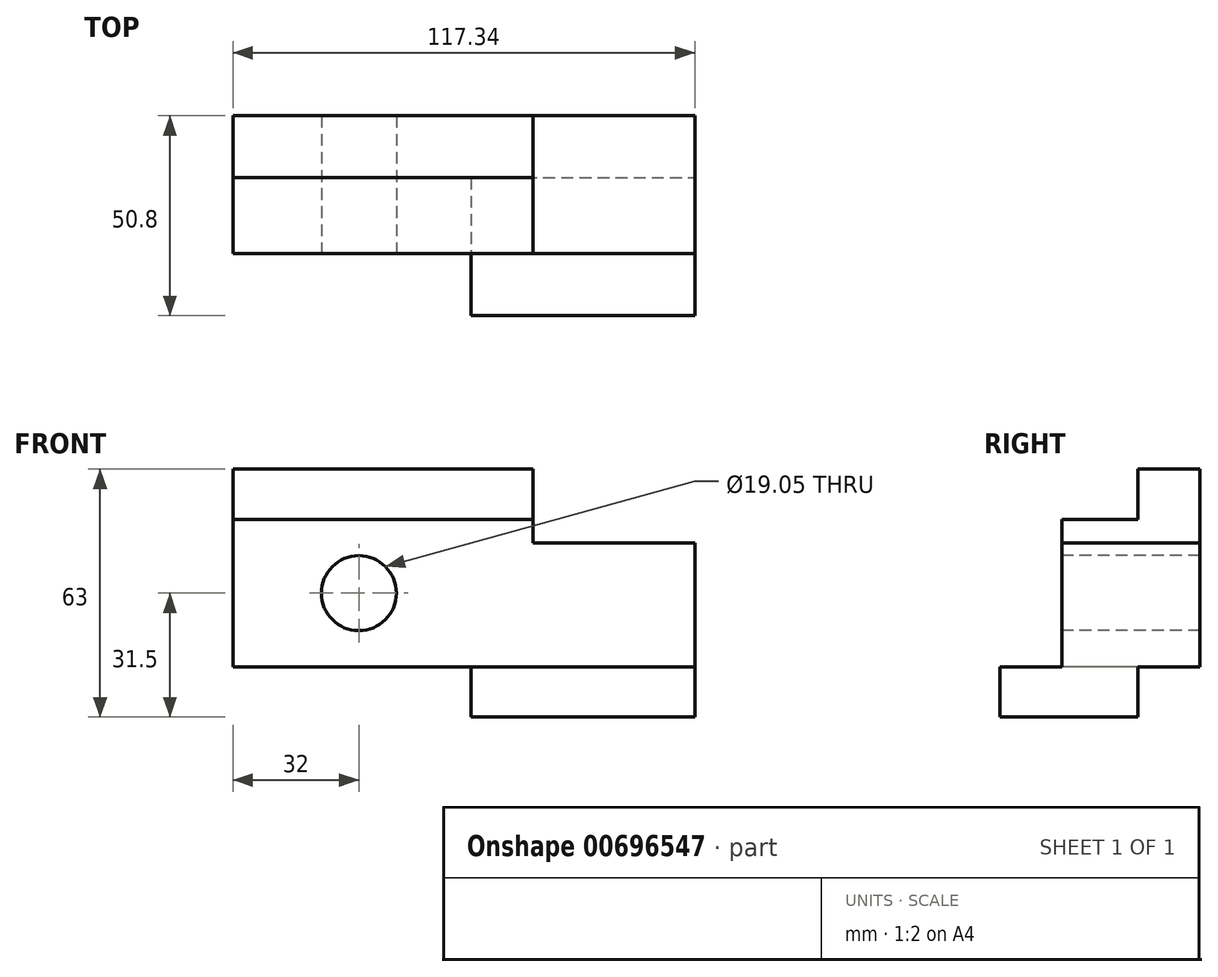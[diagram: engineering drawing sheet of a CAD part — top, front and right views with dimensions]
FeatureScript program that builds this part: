
annotation { "Feature Type Name" : "Feature", "Feature Type Description" : "" }
export const myFeature = defineFeature(function(context is Context, id is Id, definition is map)
    precondition{}
    {
        {
            var Q0;
            Q0=qCreatedBy(makeId("Front.planeOp"),FACE);
            var sketch = newSketch(context, id + "F0", { "sketchPlane" : qUnion([Q0])});
            skLineSegment(sketch, "E0.bottom", {"start": v(-58.67, 31.5) * mm, "end": v(58.67, 31.5) * mm});
            skLineSegment(sketch, "E0.top", {"start": v(-58.67, -31.5) * mm, "end": v(58.67, -31.5) * mm});
            skLineSegment(sketch, "E0.left", {"start": v(-58.67, 31.5) * mm, "end": v(-58.67, -31.5) * mm});
            skLineSegment(sketch, "E0.right", {"start": v(58.67, 31.5) * mm, "end": v(58.67, -31.5) * mm});
            skPoint(sketch, "E0.middle", {"position": v(0, 0) * mm});
            skSolve(sketch);
        }
        {
            var Q0;
            Q0=makeQuery(id+"F0.imprint","IMPRINT",FACE,{"disambiguationData":[TD([[makeQuery(id+"F0.imprint","IMPRINT",EDGE,{"derivedFrom":sQuery(id+"F0.wireOp",EDGE,"E0.bottom")}),-1.0]])]});
            extrude(context, id + "F1", {"entities" : qUnion([Q0]), "depth" : 50.8 * mm, "offsetDistance" : 25.4 * mm});
        }
        {
            var Q0;
            Q0=makeQuery(id+"F1.opExtrude","CAP_FACE",FACE,{"disambiguationData":[OSD([sQuery(id+"F0.wireOp",EDGE,"E0.bottom"),sQuery(id+"F0.wireOp",EDGE,"E0.top"),sQuery(id+"F0.wireOp",EDGE,"E0.left"),sQuery(id+"F0.wireOp",EDGE,"E0.right")])],"isStart":false});
            var sketch = newSketch(context, id + "F2", { "sketchPlane" : qUnion([Q0])});
            skLineSegment(sketch, "E1.bottom", {"start": v(58.67, 31.5) * mm, "end": v(17.53, 31.5) * mm});
            skLineSegment(sketch, "E1.top", {"start": v(58.67, 12.7) * mm, "end": v(17.53, 12.7) * mm});
            skLineSegment(sketch, "E1.left", {"start": v(58.67, 31.5) * mm, "end": v(58.67, 12.7) * mm});
            skLineSegment(sketch, "E1.right", {"start": v(17.53, 31.5) * mm, "end": v(17.53, 12.7) * mm});
            skSolve(sketch);
        }
        {
            var Q0;
            Q0=makeQuery(id+"F2.imprint","IMPRINT",FACE,{"disambiguationData":[TD([[makeQuery(id+"F2.imprint","IMPRINT",EDGE,{"derivedFrom":sQuery(id+"F2.wireOp",EDGE,"E1.bottom")}),-1.0]])]});
            extrude(context, id + "F3", {"entities" : qUnion([Q0]), "operationType" : NewBodyOperationType.REMOVE, "endBound" : BoundingType.THROUGH_ALL, "oppositeDirection" : true, "depth" : 25.4 * mm, "offsetDistance" : 25.4 * mm});
        }
        {
            var Q0;
            Q0=makeQuery(id+"F1.opExtrude","CAP_FACE",FACE,{"disambiguationData":[OSD([sQuery(id+"F0.wireOp",EDGE,"E0.bottom"),sQuery(id+"F0.wireOp",EDGE,"E0.top"),sQuery(id+"F0.wireOp",EDGE,"E0.left"),sQuery(id+"F0.wireOp",EDGE,"E0.right")])],"isStart":false});
            var sketch = newSketch(context, id + "F4", { "sketchPlane" : qUnion([Q0])});
            skLineSegment(sketch, "E2.bottom", {"start": v(-58.67, -31.5) * mm, "end": v(1.78, -31.5) * mm});
            skLineSegment(sketch, "E2.top", {"start": v(-58.67, -18.8) * mm, "end": v(1.78, -18.8) * mm});
            skLineSegment(sketch, "E2.left", {"start": v(-58.67, -31.5) * mm, "end": v(-58.67, -18.8) * mm});
            skLineSegment(sketch, "E2.right", {"start": v(1.78, -31.5) * mm, "end": v(1.78, -18.8) * mm});
            skSolve(sketch);
        }
        {
            var Q0;
            Q0=makeQuery(id+"F4.imprint","IMPRINT",FACE,{"disambiguationData":[TD([[makeQuery(id+"F4.imprint","IMPRINT",EDGE,{"derivedFrom":sQuery(id+"F4.wireOp",EDGE,"E2.bottom")}),1.0]])]});
            extrude(context, id + "F5", {"entities" : qUnion([Q0]), "operationType" : NewBodyOperationType.REMOVE, "endBound" : BoundingType.THROUGH_ALL, "oppositeDirection" : true, "depth" : 25.4 * mm, "offsetDistance" : 25.4 * mm});
        }
        {
            var Q0;
            Q0=makeQuery(id+"F3.boolean.opBoolean","COPY",FACE,{"derivedFrom":makeQuery(id+"F3.opExtrude","SWEPT_FACE",FACE,{"disambiguationData":[OSD([sQuery(id+"F2.wireOp",EDGE,"E1.right")])]})});
            var sketch = newSketch(context, id + "F6", { "sketchPlane" : qUnion([Q0])});
            skLineSegment(sketch, "E3.bottom", {"start": v(-50.8, 31.5) * mm, "end": v(-15.75, 31.5) * mm});
            skLineSegment(sketch, "E3.top", {"start": v(-50.8, 18.78) * mm, "end": v(-15.75, 18.78) * mm});
            skLineSegment(sketch, "E3.left", {"start": v(-50.8, 31.5) * mm, "end": v(-50.8, 18.78) * mm});
            skLineSegment(sketch, "E3.right", {"start": v(-15.75, 31.5) * mm, "end": v(-15.75, 18.78) * mm});
            skSolve(sketch);
        }
        {
            var Q0;
            Q0=makeQuery(id+"F6.imprint","IMPRINT",FACE,{"disambiguationData":[TD([[makeQuery(id+"F6.imprint","IMPRINT",EDGE,{"derivedFrom":sQuery(id+"F6.wireOp",EDGE,"E3.bottom")}),1.0]])]});
            extrude(context, id + "F7", {"entities" : qUnion([Q0]), "operationType" : NewBodyOperationType.REMOVE, "endBound" : BoundingType.THROUGH_ALL, "oppositeDirection" : true, "depth" : 25.4 * mm, "offsetDistance" : 25.4 * mm});
        }
        {
            var Q0;
            Q0=makeQuery(id+"F1.opExtrude","SWEPT_FACE",FACE,{"disambiguationData":[OSD([sQuery(id+"F0.wireOp",EDGE,"E0.right")])]});
            var sketch = newSketch(context, id + "F8", { "sketchPlane" : qUnion([Q0])});
            skLineSegment(sketch, "E4.bottom", {"start": v(-50.8, -18.8) * mm, "end": v(-35.04, -18.8) * mm});
            skLineSegment(sketch, "E4.top", {"start": v(-50.8, 12.7) * mm, "end": v(-35.04, 12.7) * mm});
            skLineSegment(sketch, "E4.left", {"start": v(-50.8, -18.8) * mm, "end": v(-50.8, 12.7) * mm});
            skLineSegment(sketch, "E4.right", {"start": v(-35.04, -18.8) * mm, "end": v(-35.04, 12.7) * mm});
            skSolve(sketch);
        }
        {
            var Q0;
            Q0=makeQuery(id+"F8.imprint","IMPRINT",FACE,{"disambiguationData":[TD([[makeQuery(id+"F8.imprint","IMPRINT",EDGE,{"derivedFrom":sQuery(id+"F8.wireOp",EDGE,"E4.bottom")}),1.0]])]});
            extrude(context, id + "F9", {"entities" : qUnion([Q0]), "operationType" : NewBodyOperationType.REMOVE, "endBound" : BoundingType.THROUGH_ALL, "oppositeDirection" : true, "depth" : 25.4 * mm, "offsetDistance" : 25.4 * mm});
        }
        {
            var Q0;
            Q0=makeQuery(id+"F3.boolean.opBoolean","COPY",FACE,{"derivedFrom":makeQuery(id+"F3.opExtrude","SWEPT_FACE",FACE,{"disambiguationData":[OSD([sQuery(id+"F2.wireOp",EDGE,"E1.right")])]})});
            var sketch = newSketch(context, id + "F10", { "sketchPlane" : qUnion([Q0])});
            skLineSegment(sketch, "E5.bottom", {"start": v(-50.8, 18.78) * mm, "end": v(-35.04, 18.78) * mm});
            skLineSegment(sketch, "E5.top", {"start": v(-50.8, 12.7) * mm, "end": v(-35.04, 12.7) * mm});
            skLineSegment(sketch, "E5.left", {"start": v(-50.8, 18.78) * mm, "end": v(-50.8, 12.7) * mm});
            skLineSegment(sketch, "E5.right", {"start": v(-35.04, 18.78) * mm, "end": v(-35.04, 12.7) * mm});
            skSolve(sketch);
        }
        {
            var Q0;
            Q0=makeQuery(id+"F10.imprint","IMPRINT",FACE,{"disambiguationData":[TD([[makeQuery(id+"F10.imprint","IMPRINT",EDGE,{"derivedFrom":sQuery(id+"F10.wireOp",EDGE,"E5.bottom")}),-1.0]])]});
            extrude(context, id + "F11", {"entities" : qUnion([Q0]), "operationType" : NewBodyOperationType.REMOVE, "endBound" : BoundingType.THROUGH_ALL, "oppositeDirection" : true, "depth" : 25.4 * mm, "offsetDistance" : 25.4 * mm});
        }
        {
            var Q0;
            Q0=makeQuery(id+"F1.opExtrude","SWEPT_FACE",FACE,{"disambiguationData":[OSD([sQuery(id+"F0.wireOp",EDGE,"E0.right")])]});
            var sketch = newSketch(context, id + "F12", { "sketchPlane" : qUnion([Q0])});
            skLineSegment(sketch, "E6.bottom", {"start": v(0, -31.5) * mm, "end": v(-15.75, -31.5) * mm});
            skLineSegment(sketch, "E6.top", {"start": v(0, -18.8) * mm, "end": v(-15.75, -18.8) * mm});
            skLineSegment(sketch, "E6.left", {"start": v(0, -31.5) * mm, "end": v(0, -18.8) * mm});
            skLineSegment(sketch, "E6.right", {"start": v(-15.75, -31.5) * mm, "end": v(-15.75, -18.8) * mm});
            skSolve(sketch);
        }
        {
            var Q0;
            Q0=makeQuery(id+"F12.imprint","IMPRINT",FACE,{"disambiguationData":[TD([[makeQuery(id+"F12.imprint","IMPRINT",EDGE,{"derivedFrom":sQuery(id+"F12.wireOp",EDGE,"E6.bottom")}),1.0]])]});
            extrude(context, id + "F13", {"entities" : qUnion([Q0]), "operationType" : NewBodyOperationType.REMOVE, "endBound" : BoundingType.THROUGH_ALL, "oppositeDirection" : true, "depth" : 25.4 * mm, "offsetDistance" : 25.4 * mm});
        }
        {
            var Q0;
            Q0=makeQuery(id+"F11.boolean.opBoolean","MERGE",FACE,{"derivedFrom":[makeQuery(id+"F9.boolean.opBoolean","COPY",FACE,{"derivedFrom":makeQuery(id+"F9.opExtrude","SWEPT_FACE",FACE,{"disambiguationData":[OSD([sQuery(id+"F8.wireOp",EDGE,"E4.right")])]})}),makeQuery(id+"F11.opExtrude","SWEPT_FACE",FACE,{"disambiguationData":[OSD([sQuery(id+"F10.wireOp",EDGE,"E5.right")])]})]});
            var sketch = newSketch(context, id + "F14", { "sketchPlane" : qUnion([Q0])});
            skCircle(sketch, "E7", {"center": v(-26.67, 0) * mm, "radius": 9.52 * mm});
            skSolve(sketch);
        }
        {
            var Q0;
            Q0=makeQuery(id+"F14.imprint","IMPRINT",FACE,{"disambiguationData":[TD([[makeQuery(id+"F14.imprint","IMPRINT",EDGE,{"derivedFrom":sQuery(id+"F14.wireOp",EDGE,"E7")}),1.0]])]});
            extrude(context, id + "F15", {"entities" : qUnion([Q0]), "operationType" : NewBodyOperationType.REMOVE, "endBound" : BoundingType.THROUGH_ALL, "oppositeDirection" : true, "depth" : 25.4 * mm, "offsetDistance" : 25.4 * mm});
        }
    });
